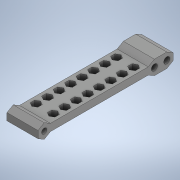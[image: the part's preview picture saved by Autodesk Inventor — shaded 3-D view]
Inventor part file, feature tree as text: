
AUTODESK INVENTOR PART (.ipt)
format: ipt  version: 2020 (Build 240168000, 168)  size: 454,656 bytes
history: native  units: in
note: dims shown in document units (in); Inventor stores cm internally (conversion verified against a paired STEP export)
features: sketch x7, extrude x6, projected_geometry x4, plane x2, mirror x1
ambient origin geometry x8: Origin, YZ Plane, XZ Plane, XY Plane, X Axis, Y Axis, Z Axis, Center Point
bodies: Solid1 (feature_tree)
feature tree (20):
  extrude  "Extrusion1"  Depth=3.4256in
  plane  "Work Plane1"
  extrude  "Extrusion2"  Depth=0.7874in
  sketch  "Sketch4"  dims[d4=0.0in d5=0.0827in]
  extrude  "Extrusion4"  Depth=0.0827in
  plane  "Work Plane2"
  extrude  "Extrusion6"  Depth=3.1106in
  mirror  "Mirror2"
  extrude  "Extrusion7"  Depth=0.315in
  extrude  "Extrusion8"  Depth=0.2362in
  sketch  "Sketch1"  dims[d0=0.1818in d1=3.4256in]
  sketch  "Sketch2"  dims[d2=0.1339in d3=0.7874in]
  sketch  "Sketch5"  dims[d6=0.7874in d7=0.0in d28=3.1106in]
  sketch  "Sketch7"  dims[d29=0.315in d31=0.315in]
  projected_geometry  "Projected Loop7"
  projected_geometry  "Projected Loop8"
  sketch  "Sketch8"  dims[d33=0.1575in d34=0.2362in]
  projected_geometry  "Projected Loop9"
  sketch  "Sketch10"  dims[d35=0.0in d38=0.315in d39=0.2756in d40=-0.3092in d41=0.0787in d42=0.0787in d43=0.0787in d44=3.1496in d46=0.2913in d47=0.3937in d49=0.3937in d51=3.1496in d53=0.2913in d54=0.3937in d56=0.3937in d58=0.0in d59=0.0in d60=150.0deg d61=0.1339in d62=0.1181in d63=1.1811in d64=0.1575in d65=0.0in]
  projected_geometry  "Projected Loop10"
